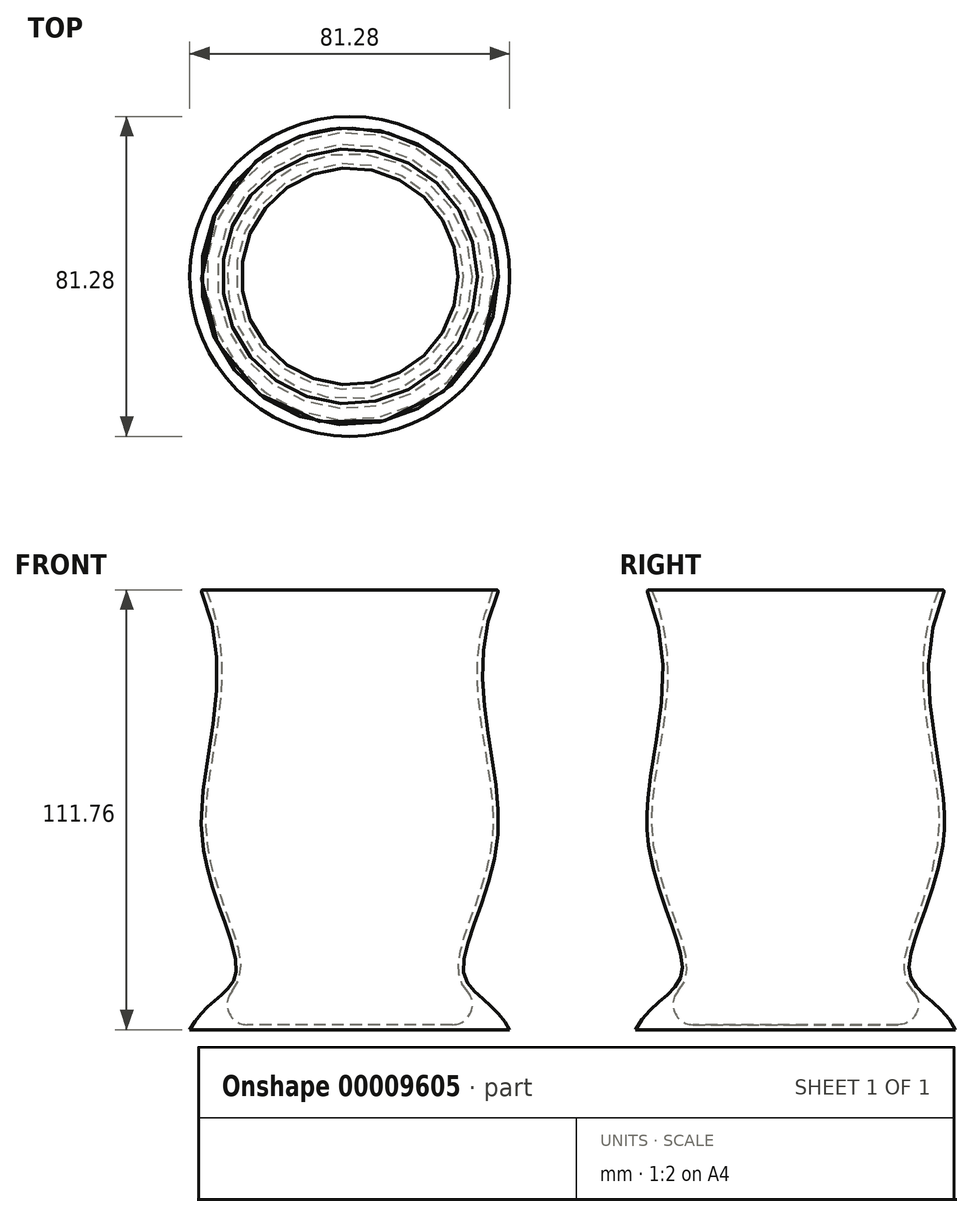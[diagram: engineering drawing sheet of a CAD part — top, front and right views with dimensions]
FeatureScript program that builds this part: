
annotation { "Feature Type Name" : "Feature", "Feature Type Description" : "" }
export const myFeature = defineFeature(function(context is Context, id is Id, definition is map)
    precondition{}
    {
        {
            var Q0;
            Q0=qCreatedBy(makeId("Front.planeOp"),FACE);
            var sketch = newSketch(context, id + "F0", { "sketchPlane" : qUnion([Q0])});
            skLineSegment(sketch, "E0", {"start": v(0, 0) * mm, "end": v(-40.64, 0) * mm});
            skFitSpline(sketch, "E1", {"points": [v(-40.64, 0) * mm, v(-35.11, 6.7) * mm, v(-28.89, 14.76) * mm, v(-37.64, 49.32) * mm, v(-37.88, 111.76) * mm], "startDerivative": vector(23, 46.75) * mm, "endDerivative": vector(-76.1, 176.35) * mm});
            skLineSegment(sketch, "E2", {"start": v(-37.88, 111.76) * mm, "end": v(0, 111.76) * mm});
            skLineSegment(sketch, "E3", {"start": v(0, 111.76) * mm, "end": v(0, 0) * mm});
            skSolve(sketch);
        }
        {
            var Q0;
            Q0=makeQuery(id+"F0.imprint","IMPRINT",FACE,{"disambiguationData":[TD([[makeQuery(id+"F0.imprint","IMPRINT",EDGE,{"derivedFrom":sQuery(id+"F0.wireOp",EDGE,"E0")}),-1.0]])]});
            var Q1;
            Q1=sQuery(id+"F0.wireOp",EDGE,"E3");
            revolve(context, id + "F1", {"entities" : qUnion([Q0]), "axis" : qUnion([Q1]), "revolveType" : RevolveType.FULL});
        }
        {
            var Q0;
            Q0=makeQuery(id+"F1.opRevolve","SWEPT_FACE",FACE,{"disambiguationData":[OSD([sQuery(id+"F0.wireOp",EDGE,"E2")])]});
            shell(context, id + "F2", {"entities" : qUnion([Q0]), "thickness" : 1.27 * mm});
        }
        {
            var Q0;
            Q0=makeQuery(id+"F1.opRevolve","SWEPT_EDGE",EDGE,{"disambiguationData":[OSD([sQuery(id+"F0.wireOp",EDGE,"E1"),sQuery(id+"F0.wireOp",EDGE,"E2")])]});
            var Q1;
            Q1=makeQuery(id+"F2.opShell","OFFSET_EDGE",EDGE,{"disambiguationData":[OSD([sQuery(id+"F0.wireOp",EDGE,"E1"),sQuery(id+"F0.wireOp",EDGE,"E2")])]});
            fillet(context, id + "F3", {"entities" : qUnion([Q0, Q1]), "radius" : 0.38 * mm, "tangentPropagation" : true, "allowEdgeOverflow" : false});
        }
        {
            var Q0;
            Q0=makeQuery(id+"F2.opShell","OFFSET_FACE",FACE,{"disambiguationData":[OSD([sQuery(id+"F0.wireOp",EDGE,"E0")])]});
            fillet(context, id + "F4", {"entities" : qUnion([Q0]), "radius" : 5.08 * mm, "tangentPropagation" : true, "allowEdgeOverflow" : false});
        }
    });
